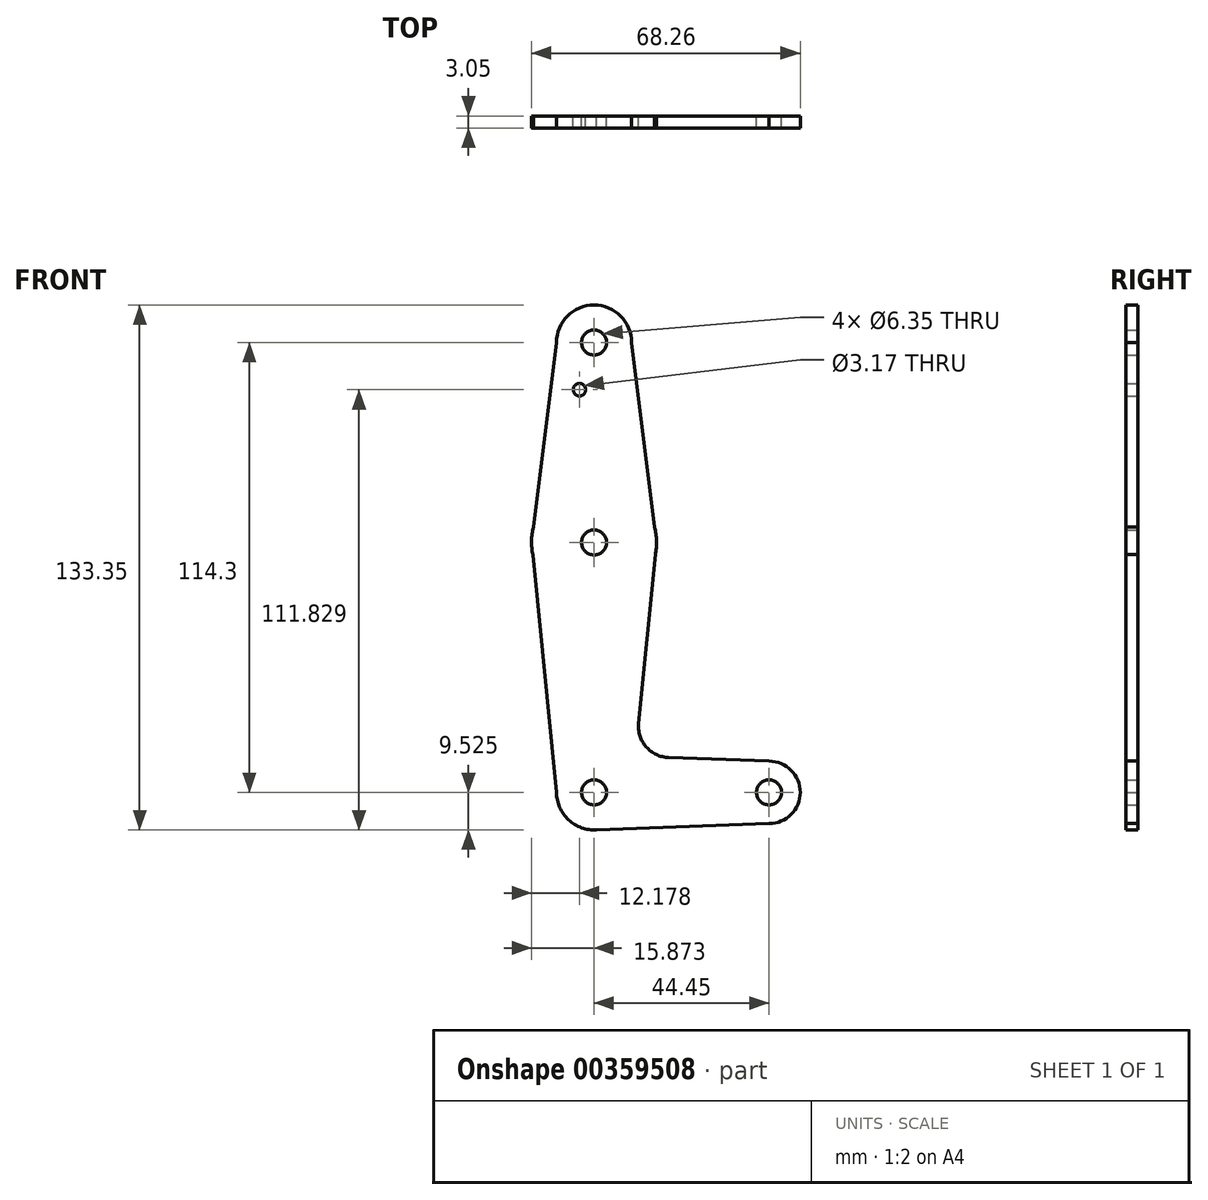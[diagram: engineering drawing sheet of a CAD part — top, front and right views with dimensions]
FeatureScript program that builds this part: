
annotation { "Feature Type Name" : "Feature", "Feature Type Description" : "" }
export const myFeature = defineFeature(function(context is Context, id is Id, definition is map)
    precondition{}
    {
        {
            var Q0;
            Q0=qCreatedBy(makeId("Front.planeOp"),FACE);
            var sketch = newSketch(context, id + "F0", { "sketchPlane" : qUnion([Q0])});
            skCircle(sketch, "E0", {"center": v(-47.59, 66.85) * mm, "radius": 9.53 * mm});
            skCircle(sketch, "E1", {"center": v(-47.59, 16.05) * mm, "radius": 15.88 * mm});
            skCircle(sketch, "E2", {"center": v(-47.59, -47.45) * mm, "radius": 9.53 * mm});
            skCircle(sketch, "E3", {"center": v(-3.14, -47.45) * mm, "radius": 7.94 * mm});
            skCircle(sketch, "E4", {"center": v(-47.59, 66.85) * mm, "radius": 3.18 * mm});
            skCircle(sketch, "E5", {"center": v(-47.59, 16.05) * mm, "radius": 3.18 * mm});
            skCircle(sketch, "E6", {"center": v(-47.59, -47.45) * mm, "radius": 3.18 * mm});
            skCircle(sketch, "E7", {"center": v(-3.14, -47.45) * mm, "radius": 3.18 * mm});
            skCircle(sketch, "E8", {"center": v(-51.28, 54.86) * mm, "radius": 1.59 * mm});
            skLineSegment(sketch, "E9", {"start": v(-47.59, -47.45) * mm, "end": v(-3.14, -47.45) * mm, "construction": true});
            skLineSegment(sketch, "E10", {"start": v(-47.59, 16.05) * mm, "end": v(-47.59, -47.45) * mm});
            skLineSegment(sketch, "E11", {"start": v(-47.59, 66.85) * mm, "end": v(-47.59, -47.45) * mm, "construction": true});
            skLineSegment(sketch, "E12", {"start": v(-38.06, 66.85) * mm, "end": v(-31.71, 16.05) * mm});
            skLineSegment(sketch, "E13", {"start": v(-31.71, 16.05) * mm, "end": v(-36.27, -29.87) * mm});
            skLineSegment(sketch, "E14", {"start": v(-57.11, 66.85) * mm, "end": v(-63.46, 16.05) * mm});
            skLineSegment(sketch, "E15", {"start": v(-63.46, 16.05) * mm, "end": v(-57.11, -47.45) * mm});
            skLineSegment(sketch, "E16", {"start": v(-28.64, -38.6) * mm, "end": v(-3.14, -39.5) * mm});
            skLineSegment(sketch, "E17", {"start": v(-47.59, -56.97) * mm, "end": v(-3.14, -55.38) * mm});
            skPoint(sketch, "E18.endSnap0", {"position": v(-25.36, -38.71) * mm});
            skPoint(sketch, "E19.newPointB", {"position": v(-47.59, -37.92) * mm});
            skArc(sketch, "E19.filletArc", {"start": v(-36.27, -29.87) * mm, "mid": v(-34.35, -35.88) * mm, "end": v(-28.64, -38.6) * mm});
            skSolve(sketch);
        }
        {
            var Q0;
            Q0 = qSketchRegion(id + "F0", true);
            extrude(context, id + "F1", {"entities" : qUnion([Q0]), "depth" : 3.05 * mm});
        }
    });
